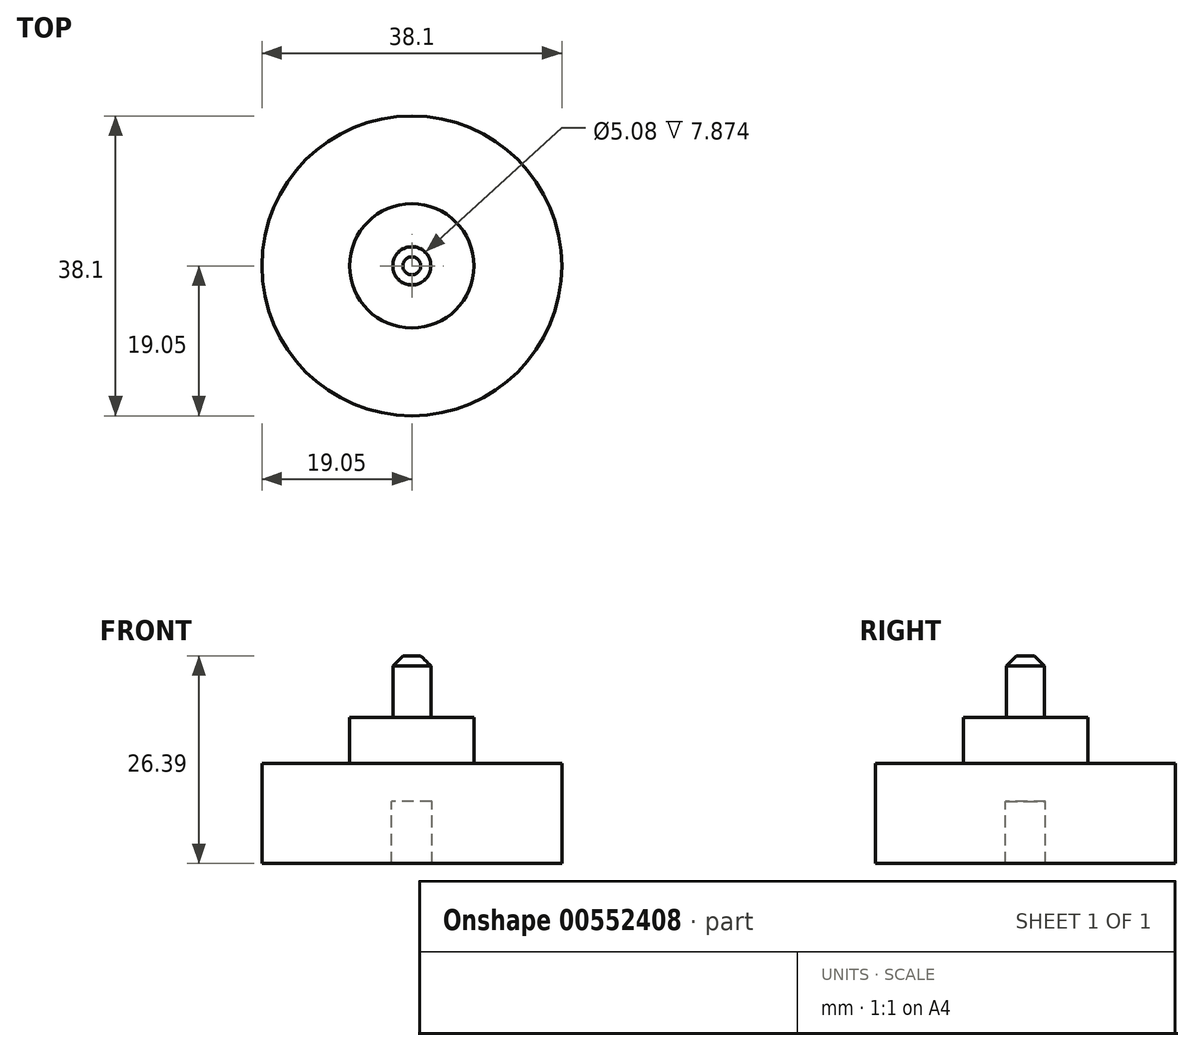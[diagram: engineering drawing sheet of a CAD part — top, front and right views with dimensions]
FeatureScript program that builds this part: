
annotation { "Feature Type Name" : "Feature", "Feature Type Description" : "" }
export const myFeature = defineFeature(function(context is Context, id is Id, definition is map)
    precondition{}
    {
        {
            var Q0;
            Q0=qCreatedBy(makeId("Front.planeOp"),FACE);
            var sketch = newSketch(context, id + "F0", { "sketchPlane" : qUnion([Q0])});
            skLineSegment(sketch, "E0", {"start": v(19.05, 0) * mm, "end": v(19.05, 12.7) * mm});
            skLineSegment(sketch, "E1", {"start": v(19.05, 12.7) * mm, "end": v(7.9, 12.7) * mm});
            skLineSegment(sketch, "E2", {"start": v(2.41, 18.54) * mm, "end": v(7.9, 18.54) * mm});
            skLineSegment(sketch, "E3", {"start": v(7.9, 18.54) * mm, "end": v(7.9, 12.7) * mm});
            skLineSegment(sketch, "E4", {"start": v(2.54, 0) * mm, "end": v(2.54, 7.87) * mm});
            skLineSegment(sketch, "E5", {"start": v(2.54, 7.87) * mm, "end": v(0, 7.87) * mm});
            skLineSegment(sketch, "E6", {"start": v(0, 26.4) * mm, "end": v(2.41, 26.4) * mm});
            skLineSegment(sketch, "E7", {"start": v(2.41, 26.4) * mm, "end": v(2.41, 18.54) * mm});
            skPoint(sketch, "E8.start.orphan", {"position": v(0, 12.7) * mm});
            skPoint(sketch, "E9.start.orphan", {"position": v(0, 18.54) * mm});
            skLineSegment(sketch, "E10", {"start": v(0, 26.4) * mm, "end": v(0, 7.87) * mm});
            skLineSegment(sketch, "E11", {"start": v(2.54, 0) * mm, "end": v(19.05, 0) * mm});
            skSolve(sketch);
        }
        {
            var Q0;
            Q0 = qSketchRegion(id + "F0", true);
            var Q1;
            Q1=sQuery(id+"F0.wireOp",EDGE,"E10");
            revolve(context, id + "F1", {"entities" : qUnion([Q0]), "axis" : qUnion([Q1]), "revolveType" : RevolveType.FULL});
        }
        {
            var Q0;
            Q0=makeQuery(id+"F1.opRevolve","SWEPT_EDGE",EDGE,{"disambiguationData":[OSD([sQuery(id+"F0.wireOp",EDGE,"E6"),sQuery(id+"F0.wireOp",EDGE,"E7")])]});
            chamfer(context, id + "F2", {"entities" : qUnion([Q0]), "width" : 1.27 * mm, "tangentPropagation" : true});
        }
    });
